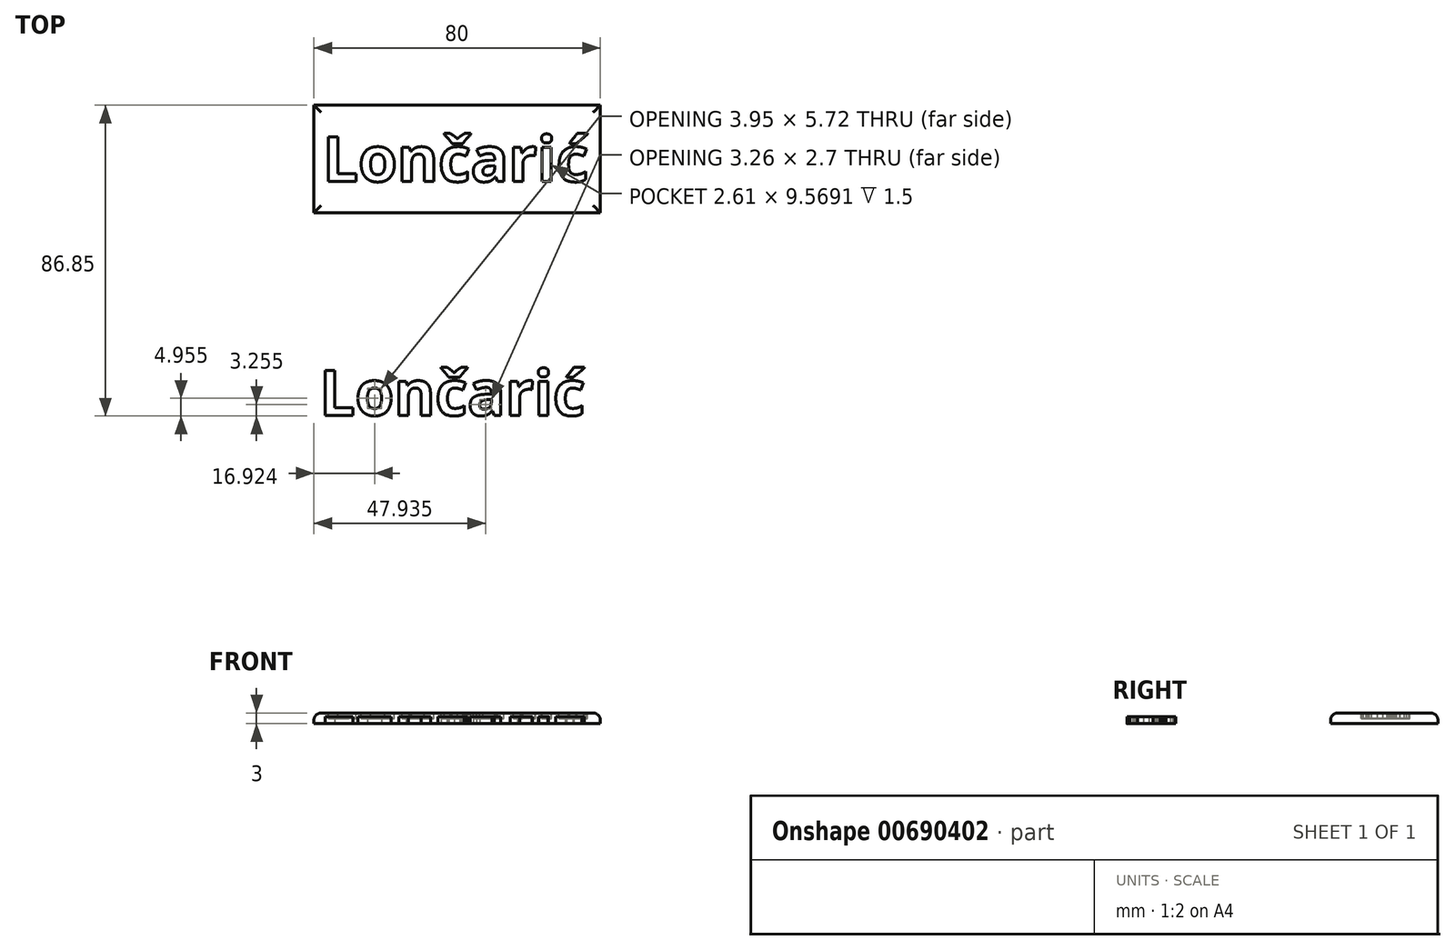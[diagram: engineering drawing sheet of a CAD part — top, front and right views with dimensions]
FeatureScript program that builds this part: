
annotation { "Feature Type Name" : "Feature", "Feature Type Description" : "" }
export const myFeature = defineFeature(function(context is Context, id is Id, definition is map)
    precondition{}
    {
        {
            var Q0;
            Q0=qCreatedBy(makeId("Top.planeOp"),FACE);
            var sketch = newSketch(context, id + "F0", { "sketchPlane" : qUnion([Q0])});
            skLineSegment(sketch, "E0", {"start": v(0, 0) * mm, "end": v(0, -15) * mm, "construction": true});
            skLineSegment(sketch, "E1", {"start": v(0, -15) * mm, "end": v(-40, -15) * mm});
            skLineSegment(sketch, "E2", {"start": v(-40, -15) * mm, "end": v(-40, 15) * mm});
            skLineSegment(sketch, "E3", {"start": v(-40, 15) * mm, "end": v(40, 15) * mm});
            skLineSegment(sketch, "E4", {"start": v(40, 15) * mm, "end": v(40, -15) * mm});
            skLineSegment(sketch, "E5", {"start": v(40, -15) * mm, "end": v(0, -15) * mm});
            skSolve(sketch);
        }
        {
            var Q0;
            Q0=makeQuery(id+"F0.imprint","IMPRINT",FACE,{"disambiguationData":[TD([[makeQuery(id+"F0.imprint","IMPRINT",EDGE,{"derivedFrom":sQuery(id+"F0.wireOp",EDGE,"E1")}),-1.0]])]});
            extrude(context, id + "F1", {"entities" : qUnion([Q0]), "depth" : 3 * mm, "offsetDistance" : 25 * mm});
        }
        {
            var Q0;
            Q0=makeQuery(id+"F1.opExtrude","CAP_EDGE",EDGE,{"disambiguationData":[OSD([sQuery(id+"F0.wireOp",EDGE,"E3")])],"isStart":false});
            var Q1;
            Q1=makeQuery(id+"F1.opExtrude","CAP_EDGE",EDGE,{"disambiguationData":[OSD([sQuery(id+"F0.wireOp",EDGE,"E2")])],"isStart":false});
            var Q2;
            Q2=makeQuery(id+"F1.opExtrude","CAP_EDGE",EDGE,{"disambiguationData":[OSD([sQuery(id+"F0.wireOp",EDGE,"E1"),sQuery(id+"F0.wireOp",EDGE,"E5")])],"isStart":false});
            var Q3;
            Q3=makeQuery(id+"F1.opExtrude","CAP_EDGE",EDGE,{"disambiguationData":[OSD([sQuery(id+"F0.wireOp",EDGE,"E4")])],"isStart":false});
            fillet(context, id + "F2", {"entities" : qUnion([Q0, Q1, Q2, Q3]), "radius" : 2 * mm, "tangentPropagation" : true, "allowEdgeOverflow" : false});
        }
        {
            var Q0;
            Q0=makeQuery(id+"F1.opExtrude","CAP_FACE",FACE,{"disambiguationData":[OSD([sQuery(id+"F0.wireOp",EDGE,"E1"),sQuery(id+"F0.wireOp",EDGE,"E2"),sQuery(id+"F0.wireOp",EDGE,"E3"),sQuery(id+"F0.wireOp",EDGE,"E4"),sQuery(id+"F0.wireOp",EDGE,"E5")])],"isStart":false});
            var sketch = newSketch(context, id + "F3", { "sketchPlane" : qUnion([Q0])});
            skText(sketch, "E6", { "text": "Lončarić", "fontName": "OpenSans-Bold.ttf"});
            const initialGuessF3  = {"E6": [-0.0375, -0.00631, 1, 0, 0.01262]};
            skSetInitialGuess(sketch, initialGuessF3);
            skSolve(sketch);
        }
        {
            var Q0;
            Q0 = qSketchRegion(id + "F3", true);
            extrude(context, id + "F4", {"entities" : qUnion([Q0]), "operationType" : NewBodyOperationType.REMOVE, "oppositeDirection" : true, "depth" : 1.5 * mm, "offsetDistance" : 25 * mm});
        }
        {
            var Q0;
            Q0=qCreatedBy(makeId("Top.planeOp"),FACE);
            var sketch = newSketch(context, id + "F5", { "sketchPlane" : qUnion([Q0])});
            skText(sketch, "E7", { "text": "Lončarić", "fontName": "OpenSans-Bold.ttf"});
            const initialGuessF5  = {"E7": [-0.0384, -0.07168, 1, 0, 0.01262]};
            skSetInitialGuess(sketch, initialGuessF5);
            skSolve(sketch);
        }
        {
            var Q0;
            Q0 = qSketchRegion(id + "F5", true);
            extrude(context, id + "F6", {"entities" : qUnion([Q0]), "depth" : 2 * mm, "offsetDistance" : 25 * mm});
        }
    });
